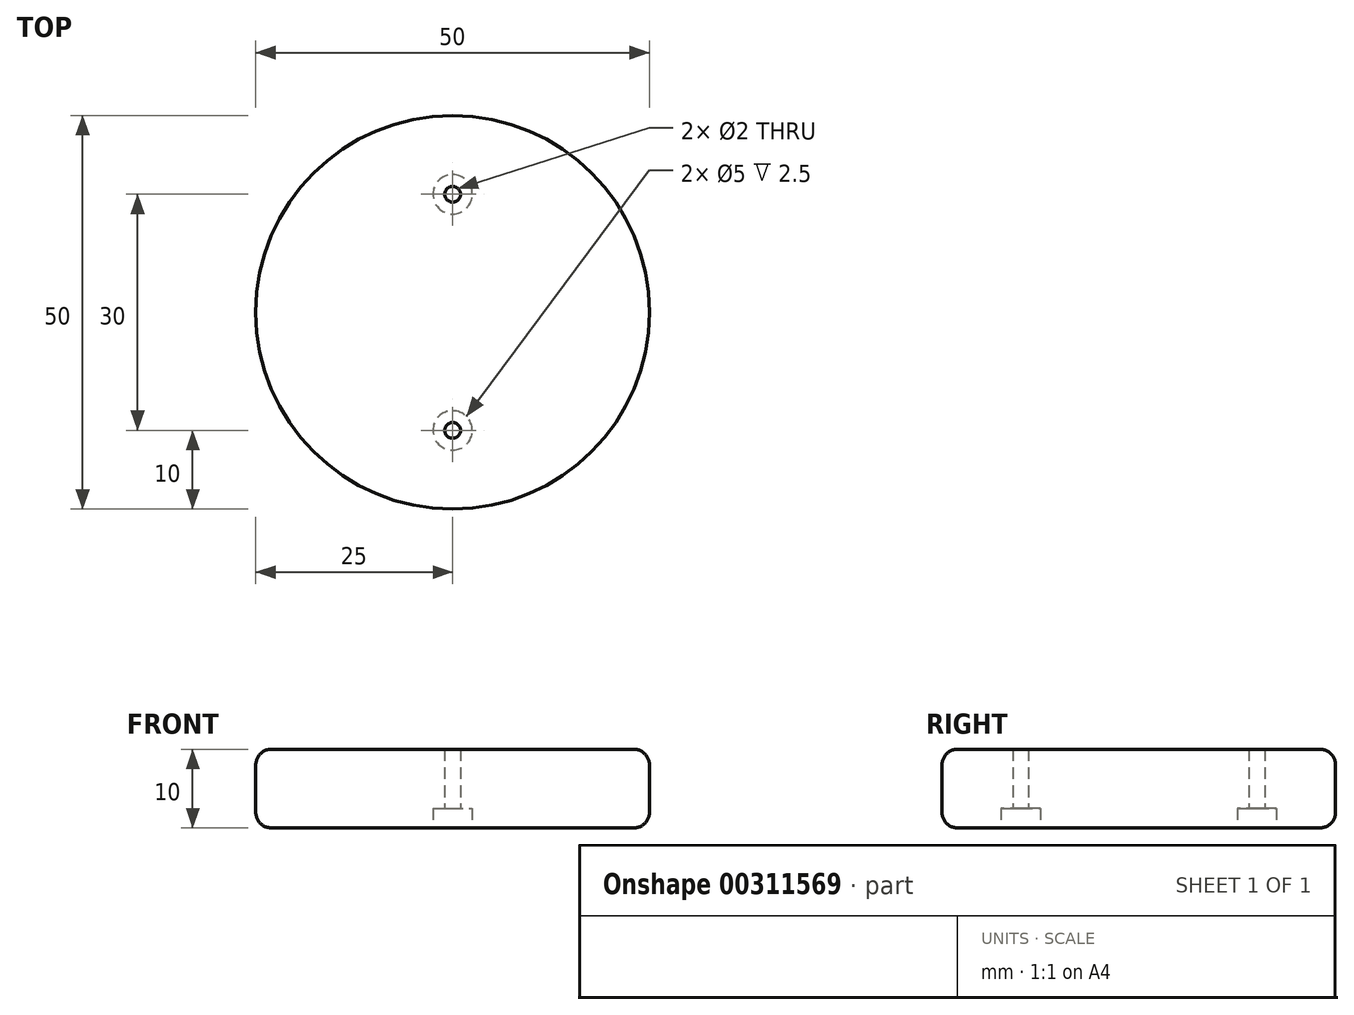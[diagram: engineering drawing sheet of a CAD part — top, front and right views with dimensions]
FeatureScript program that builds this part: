
annotation { "Feature Type Name" : "Feature", "Feature Type Description" : "" }
export const myFeature = defineFeature(function(context is Context, id is Id, definition is map)
    precondition{}
    {
        {
            var Q0;
            Q0=qCreatedBy(makeId("Top.planeOp"),FACE);
            var sketch = newSketch(context, id + "F0", { "sketchPlane" : qUnion([Q0])});
            skCircle(sketch, "E0", {"center": v(0, 0) * mm, "radius": 25 * mm});
            skSolve(sketch);
        }
        {
            var Q0;
            Q0=qSketchRegion(id+"F0",true);
            extrude(context, id + "F1", {"entities" : qUnion([Q0]), "depth" : 10 * mm});
        }
        {
            var Q0;
            Q0=makeQuery(id+"F1.opExtrude","CAP_EDGE",EDGE,{"disambiguationData":[OSD([sQuery(id+"F0.wireOp",EDGE,"E0")])],"isStart":false});
            var Q1;
            Q1=makeQuery(id+"F1.opExtrude","CAP_EDGE",EDGE,{"disambiguationData":[OSD([sQuery(id+"F0.wireOp",EDGE,"E0")])],"isStart":true});
            fillet(context, id + "F2", {"entities" : qUnion([Q0, Q1]), "radius" : 2 * mm, "tangentPropagation" : true, "allowEdgeOverflow" : false});
        }
        {
            var Q0;
            Q0=makeQuery(id+"F1.opExtrude","CAP_FACE",FACE,{"disambiguationData":[OSD([sQuery(id+"F0.wireOp",EDGE,"E0")])],"isStart":true});
            var sketch = newSketch(context, id + "F3", { "sketchPlane" : qUnion([Q0])});
            skPoint(sketch, "E1", {"position": v(0, 15) * mm});
            skPoint(sketch, "E2", {"position": v(0, -15) * mm});
            skSolve(sketch);
        }
        {
            var Q0;
            Q0=sQuery(id+"F3.wireOp",VERTEX,"E1");
            var Q1;
            Q1=sQuery(id+"F3.wireOp",VERTEX,"E2");
            var Q2;
            Q2=makeQuery(id+"F1.opExtrude","SWEPT_BODY",BODY,{"disambiguationData":[OSD([sQuery(id+"F0.wireOp",EDGE,"E0")])]});
            hole(context, id + "F4", {"style" : HoleStyle.C_BORE, "endStyle" : HoleEndStyle.THROUGH, "holeDiameter" : 2 * mm, "cBoreDiameter" : 5 * mm, "cBoreDepth" : 2.5 * mm, "startFromSketch" : true, "locations" : qUnion([Q0, Q1]), "scope" : qUnion([Q2]), "isTappedThrough" : true});
        }
    });
